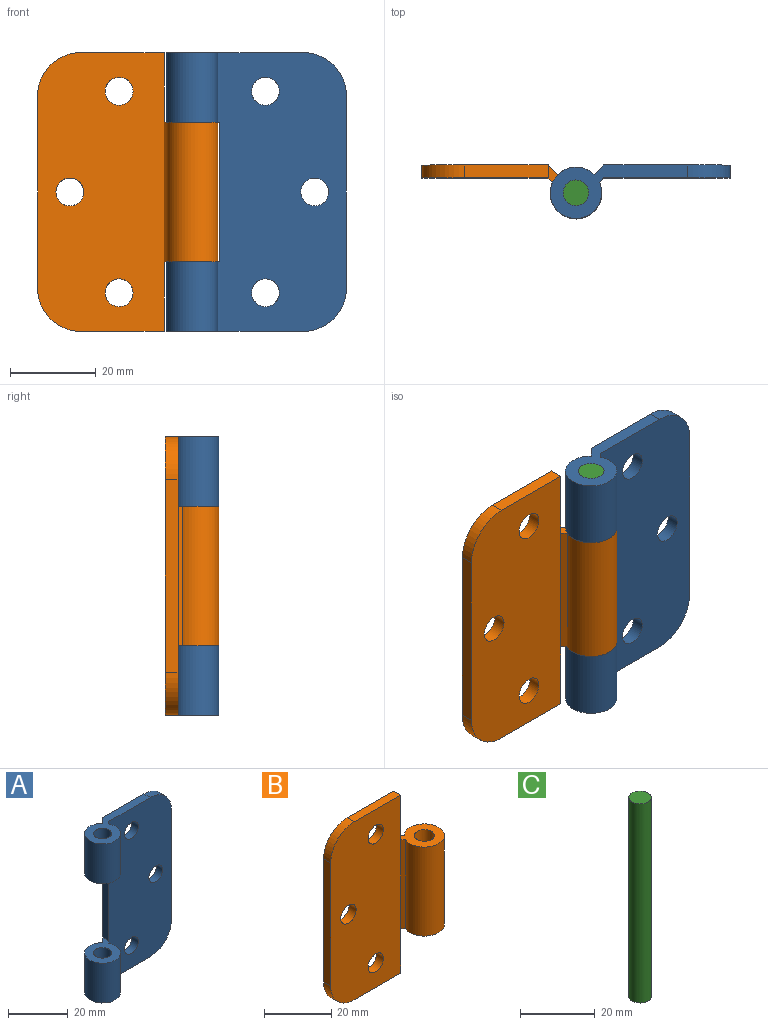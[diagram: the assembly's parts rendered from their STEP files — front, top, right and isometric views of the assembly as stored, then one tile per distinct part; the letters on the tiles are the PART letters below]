
ASSEMBLY  parts=3 mates=2
PART A: 21 faces, bbox 42x12.5x65 mm
  f0: plane 16.25x2.26mm, normal (-0.71,0.71,0), area 51.9mm2, adj f2,f6,f12,f14
  f1: plane 16.25x1.03mm, normal (0.71,-0.71,0), area 23.7mm2, adj f2,f4,f12,f14
  f2: cylinder r=6mm len=16.25mm, axis (0,0,-1), area 577.4mm2, adj f0,f1,f12,f14
  f3: cylinder r=3mm len=16.25mm, axis (0,0,-1), area 306.3mm2, adj f12,f14
  f4: plane 65x29.5mm, normal (0,-1,0), area 1775mm2, adj f1,f5,f9,f11,f12,f13,f16,f17
  f5: plane 45x3mm, normal (1,0,0), area 135mm2, adj f4,f6,f16,f17
  f6: plane 65x29.5mm, normal (0,1,0), area 1775mm2, adj f0,f5,f7,f11,f12,f13,f16,f17
  f7: plane 16.25x2.26mm, normal (-0.71,0.71,0), area 51.9mm2, adj f6,f8,f11,f15
  f8: cylinder r=6mm len=16.25mm, axis (0,0,-1), area 577.4mm2, adj f7,f9,f11,f15
  f9: plane 16.25x1.03mm, normal (0.71,-0.71,0), area 23.7mm2, adj f4,f8,f11,f15
  f10: cylinder r=3mm len=16.25mm, axis (0,0,-1), area 306.3mm2, adj f11,f15
  f11: plane 32x12.5mm, normal (0,0,1), area 148.1mm2, adj f4,f6,f7,f8,f9,f10,f17
  f12: plane 32x12.5mm, normal (0,0,-1), area 148.1mm2, adj f0,f1,f2,f3,f4,f6,f16
  f13: plane 32.5x3mm, normal (-1,0,0), area 97.5mm2, adj f4,f6,f14,f15
  f14: plane 12.5x12.5mm, normal (0,0,1), area 89.6mm2, adj f0,f1,f2,f3,f13
  f15: plane 12.5x12.5mm, normal (0,0,-1), area 89.6mm2, adj f7,f8,f9,f10,f13
  f16: cylinder r=10mm len=10mm, axis (0,1,0), area 47.1mm2, adj f4,f5,f6,f12
  f17: cylinder r=10mm len=10mm, axis (0,-1,0), area 47.1mm2, adj f4,f5,f6,f11
  f18: cylinder r=3.25mm len=6.5mm, axis (0,-1,0), area 61.3mm2, adj f4,f6
  f19: cylinder r=3.25mm len=6.5mm, axis (0,-1,0), area 61.3mm2, adj f4,f6
  f20: cylinder r=3.25mm len=6.5mm, axis (0,-1,0), area 61.3mm2, adj f4,f6
PART B: 18 faces, bbox 42x12.5x65 mm
  f0: cylinder r=6mm len=32.5mm, axis (0,0,-1), area 1154.8mm2, adj f2,f3,f4,f5
  f1: cylinder r=3mm len=32.5mm, axis (0,0,-1), area 612.6mm2, adj f2,f3
  f2: plane 12.5x12.5mm, normal (0,0,1), area 89.6mm2, adj f0,f1,f4,f5,f6
  f3: plane 12.5x12.5mm, normal (0,0,-1), area 89.6mm2, adj f0,f1,f4,f5,f7
  f4: plane 32.5x2.26mm, normal (0.71,0.71,0), area 103.8mm2, adj f0,f2,f3,f8
  f5: plane 32.5x1.03mm, normal (-0.71,-0.71,0), area 47.4mm2, adj f0,f2,f3,f10
  f6: plane 16.25x3mm, normal (1,0,0), area 48.7mm2, adj f2,f8,f10,f11
  f7: plane 16.25x3mm, normal (1,0,0), area 48.7mm2, adj f3,f8,f10,f12
  f8: plane 65x29.5mm, normal (0,1,0), area 1775mm2, adj f4,f6,f7,f9,f11,f12,f13,f14
  f9: plane 45x3mm, normal (-1,0,0), area 135mm2, adj f8,f10,f13,f14
  f10: plane 65x29.5mm, normal (0,-1,0), area 1775mm2, adj f5,f6,f7,f9,f11,f12,f13,f14
  f11: plane 19.5x3mm, normal (0,0,1), area 58.5mm2, adj f6,f8,f10,f14
  f12: plane 19.5x3mm, normal (0,0,-1), area 58.5mm2, adj f7,f8,f10,f13
  f13: cylinder r=10mm len=10mm, axis (0,-1,0), area 47.1mm2, adj f8,f9,f10,f12
  f14: cylinder r=10mm len=10mm, axis (0,1,0), area 47.1mm2, adj f8,f9,f10,f11
  f15: cylinder r=3.25mm len=6.5mm, axis (0,-1,0), area 61.3mm2, adj f8,f10
  f16: cylinder r=3.25mm len=6.5mm, axis (0,-1,0), area 61.3mm2, adj f8,f10
  f17: cylinder r=3.25mm len=6.5mm, axis (0,-1,0), area 61.3mm2, adj f8,f10
PART C: 3 faces, bbox 6x6x65 mm
  f0: cylinder r=3mm len=65mm, axis (0,0,-1), area 1225.2mm2, adj f1,f2
  f1: plane 6x6mm, normal (0,0,1), area 28.3mm2, adj f0
  f2: plane 6x6mm, normal (0,0,-1), area 28.3mm2, adj f0
PLACE A t=(-10.21,7.85,-6.76)mm
PLACE B t=(-22.25,4.31,-6.76)mm
PLACE C t=(-22.25,4.31,-6.76)mm
MATE revolute A.f2 <-> B.f0  axis (0,0,-1) through (-22.25,4.31,9.49)mm
MATE pin_slot C.f0 <-> A.f2  axis (0,0,1) through (-22.25,4.31,25.74)mm
